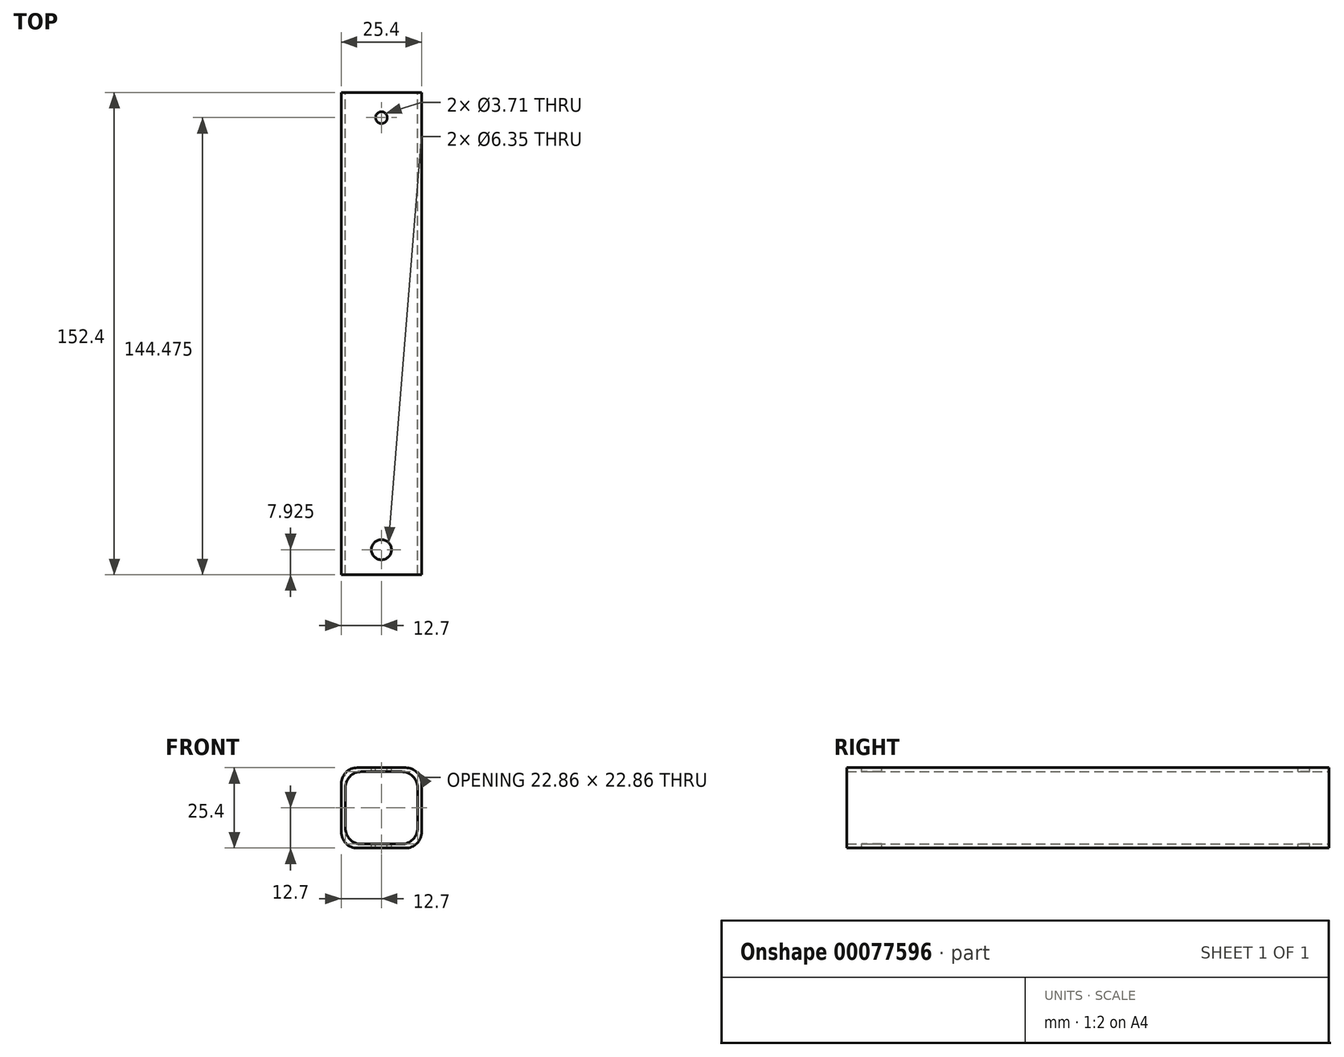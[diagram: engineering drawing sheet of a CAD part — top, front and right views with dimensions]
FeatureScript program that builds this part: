
annotation { "Feature Type Name" : "Feature", "Feature Type Description" : "" }
export const myFeature = defineFeature(function(context is Context, id is Id, definition is map)
    precondition{}
    {
        {
            var Q0;
            Q0=qCreatedBy(makeId("Front.planeOp"),FACE);
            var sketch = newSketch(context, id + "F0", { "sketchPlane" : qUnion([Q0])});
            skLineSegment(sketch, "E0.bottom", {"start": v(-12.7, 12.7) * mm, "end": v(12.7, 12.7) * mm});
            skLineSegment(sketch, "E0.top", {"start": v(-12.7, -12.7) * mm, "end": v(12.7, -12.7) * mm});
            skLineSegment(sketch, "E0.left", {"start": v(-12.7, 12.7) * mm, "end": v(-12.7, -12.7) * mm});
            skLineSegment(sketch, "E0.right", {"start": v(12.7, 12.7) * mm, "end": v(12.7, -12.7) * mm});
            skLineSegment(sketch, "E1.0", {"start": v(-11.43, 11.43) * mm, "end": v(11.43, 11.43) * mm});
            skLineSegment(sketch, "E1.1", {"start": v(-11.43, 11.43) * mm, "end": v(-11.43, -11.43) * mm});
            skLineSegment(sketch, "E1.2", {"start": v(-11.43, -11.43) * mm, "end": v(11.43, -11.43) * mm});
            skLineSegment(sketch, "E1.3", {"start": v(11.43, 11.43) * mm, "end": v(11.43, -11.43) * mm});
            skSolve(sketch);
        }
        {
            var Q0;
            Q0 = qSketchRegion(id + "F0", true);
            extrude(context, id + "F1", {"entities" : qUnion([Q0]), "depth" : 152.4 * mm});
        }
        {
            var Q0;
            Q0=makeQuery(id+"F1.opExtrude","SWEPT_EDGE",EDGE,{"disambiguationData":[OSD([sQuery(id+"F0.wireOp",EDGE,"E0.bottom"),sQuery(id+"F0.wireOp",EDGE,"E0.right")])]});
            var Q1;
            Q1=makeQuery(id+"F1.opExtrude","SWEPT_EDGE",EDGE,{"disambiguationData":[OSD([sQuery(id+"F0.wireOp",EDGE,"E0.bottom"),sQuery(id+"F0.wireOp",EDGE,"E0.left")])]});
            var Q2;
            Q2=makeQuery(id+"F1.opExtrude","SWEPT_EDGE",EDGE,{"disambiguationData":[OSD([sQuery(id+"F0.wireOp",EDGE,"E0.top"),sQuery(id+"F0.wireOp",EDGE,"E0.right")])]});
            var Q3;
            Q3=makeQuery(id+"F1.opExtrude","SWEPT_EDGE",EDGE,{"disambiguationData":[OSD([sQuery(id+"F0.wireOp",EDGE,"E0.top"),sQuery(id+"F0.wireOp",EDGE,"E0.left")])]});
            var Q4;
            Q4=makeQuery(id+"F1.opExtrude","SWEPT_EDGE",EDGE,{"disambiguationData":[OSD([sQuery(id+"F0.wireOp",EDGE,"E1.0"),sQuery(id+"F0.wireOp",EDGE,"E1.3")])]});
            var Q5;
            Q5=makeQuery(id+"F1.opExtrude","SWEPT_EDGE",EDGE,{"disambiguationData":[OSD([sQuery(id+"F0.wireOp",EDGE,"E1.0"),sQuery(id+"F0.wireOp",EDGE,"E1.1")])]});
            var Q6;
            Q6=makeQuery(id+"F1.opExtrude","SWEPT_EDGE",EDGE,{"disambiguationData":[OSD([sQuery(id+"F0.wireOp",EDGE,"E1.2"),sQuery(id+"F0.wireOp",EDGE,"E1.3")])]});
            var Q7;
            Q7=makeQuery(id+"F1.opExtrude","SWEPT_EDGE",EDGE,{"disambiguationData":[OSD([sQuery(id+"F0.wireOp",EDGE,"E1.1"),sQuery(id+"F0.wireOp",EDGE,"E1.2")])]});
            fillet(context, id + "F2", {"entities" : qUnion([Q0, Q1, Q2, Q3, Q4, Q5, Q6, Q7]), "radius" : 5.08 * mm, "tangentPropagation" : true, "allowEdgeOverflow" : false});
        }
        {
            var Q0;
            Q0=makeQuery(id+"F1.opExtrude","SWEPT_FACE",FACE,{"disambiguationData":[OSD([sQuery(id+"F0.wireOp",EDGE,"E0.bottom")])]});
            var sketch = newSketch(context, id + "F3", { "sketchPlane" : qUnion([Q0])});
            skCircle(sketch, "E2", {"center": v(0, -7.92) * mm, "radius": 1.86 * mm});
            skSolve(sketch);
        }
        {
            var Q0;
            Q0 = qSketchRegion(id + "F3", true);
            extrude(context, id + "F4", {"entities" : qUnion([Q0]), "operationType" : NewBodyOperationType.REMOVE, "endBound" : BoundingType.THROUGH_ALL, "oppositeDirection" : true, "depth" : 25.4 * mm});
        }
        {
            var Q0;
            Q0=makeQuery(id+"F1.opExtrude","SWEPT_FACE",FACE,{"disambiguationData":[OSD([sQuery(id+"F0.wireOp",EDGE,"E0.bottom")])]});
            var sketch = newSketch(context, id + "F5", { "sketchPlane" : qUnion([Q0])});
            skSolve(sketch);
        }
        {
            var Q0;
            {var subQ0=sQuery(id+"F0.wireOp",EDGE,"E0.bottom");Q0=makeQuery(id+"F5.imprint","IMPRINT",FACE,{"disambiguationData":[TD([[makeQuery(id+"F5.imprint","IMPRINT",EDGE,{"derivedFrom":makeQuery(id+"F1.opExtrude","CAP_EDGE",EDGE,{"disambiguationData":[OSD([subQ0])],"isStart":true})}),-1.0]])]});}
            var sketch = newSketch(context, id + "F6", { "sketchPlane" : qUnion([Q0])});
            skCircle(sketch, "E3", {"center": v(0, -144.48) * mm, "radius": 3.18 * mm});
            skSolve(sketch);
        }
        {
            var Q0;
            Q0 = qSketchRegion(id + "F6", true);
            extrude(context, id + "F7", {"entities" : qUnion([Q0]), "operationType" : NewBodyOperationType.REMOVE, "endBound" : BoundingType.THROUGH_ALL, "oppositeDirection" : true, "depth" : 25.4 * mm});
        }
    });
